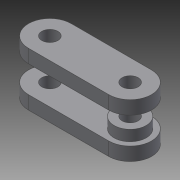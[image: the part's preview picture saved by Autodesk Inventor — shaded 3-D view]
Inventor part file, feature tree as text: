
AUTODESK INVENTOR PART (.ipt)
format: ipt  version: 2018 (Build 220112000, 112)  size: 120,320 bytes
history: native  units: mm
features: extrude x4, sketch x4, other x1, projected_geometry x1
ambient origin geometry x8: Origin, YZ Plane, XZ Plane, XY Plane, X Axis, Y Axis, Z Axis, Center Point
bodies: Body1 (feature_tree)
feature tree (10):
  other  "ソリッド1"
  extrude  "押し出し1"  Depth=4.0mm
  extrude  "押し出し2"  Depth=15.0mm
  extrude  "押し出し3"  Depth=10.0mm TaperAngle=0.0deg
  extrude  "押し出し4"  Depth=5.0mm TaperAngle=0.0deg
  sketch  "スケッチ1"
  sketch  "スケッチ2"
  projected_geometry  "投影ループ1"
  sketch  "スケッチ3"
  sketch  "スケッチ4"
